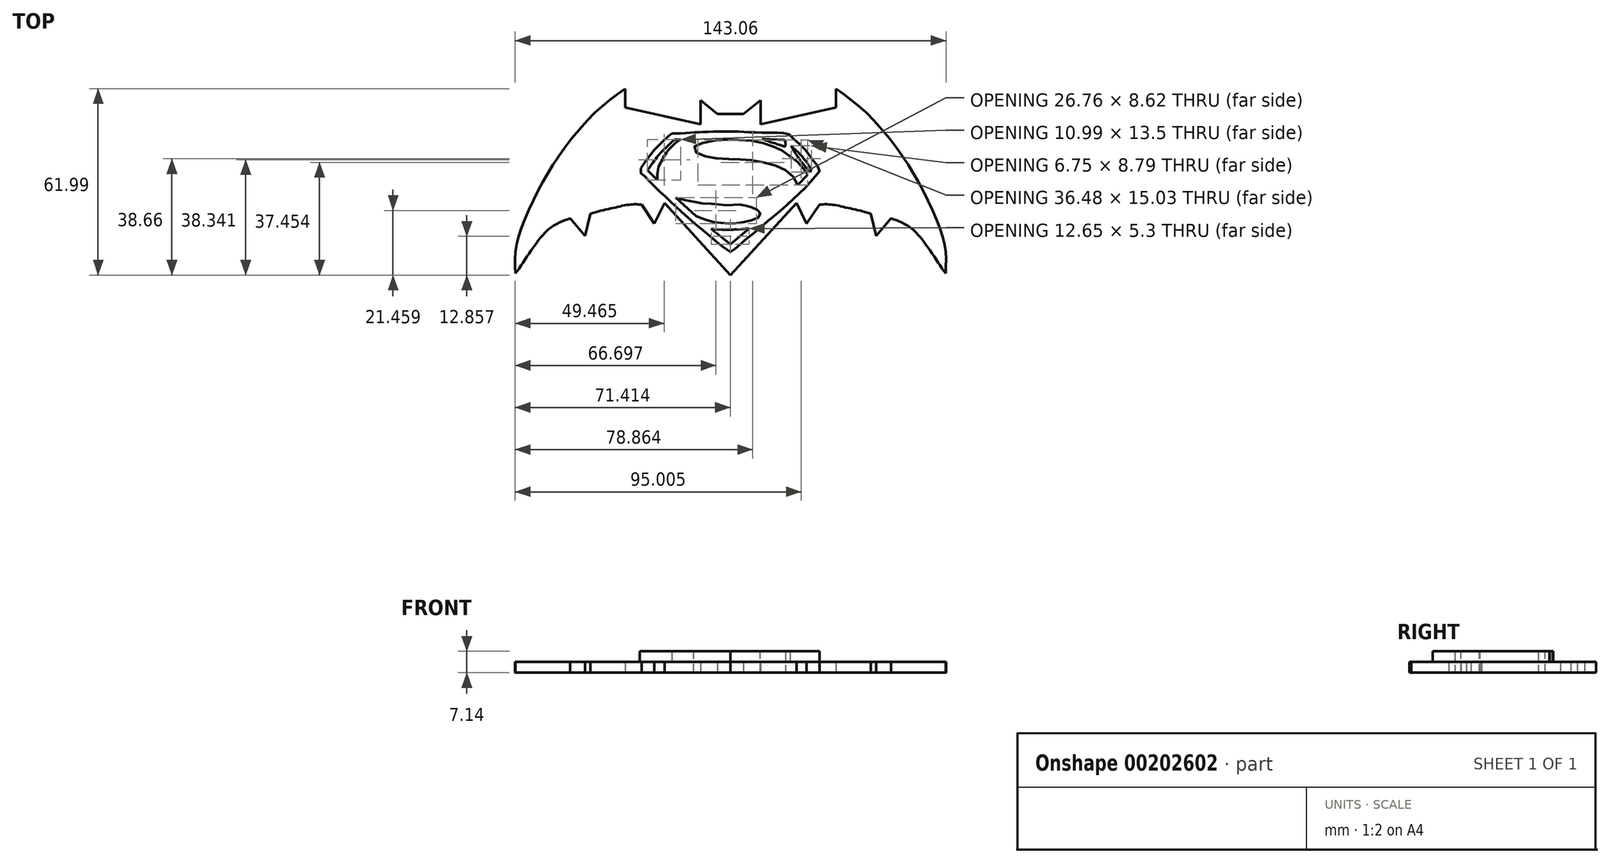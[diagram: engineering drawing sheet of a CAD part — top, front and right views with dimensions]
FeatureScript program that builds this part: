
annotation { "Feature Type Name" : "Feature", "Feature Type Description" : "" }
export const myFeature = defineFeature(function(context is Context, id is Id, definition is map)
    precondition{}
    {
        {
            var Q0;
            Q0=qCreatedBy(makeId("Top.planeOp"),FACE);
            var sketch = newSketch(context, id + "F0", { "sketchPlane" : qUnion([Q0])});
            skLineSegment(sketch, "E0", {"start": v(0, -29.29) * mm, "end": v(-21.94, -5.3) * mm});
            skLineSegment(sketch, "E1", {"start": v(-21.94, -5.3) * mm, "end": v(-25.27, -12.15) * mm});
            skLineSegment(sketch, "E2", {"start": v(-25.27, -12.15) * mm, "end": v(-29.54, -5.84) * mm});
            skFitSpline(sketch, "E3", {"points": [v(-29.54, -5.84) * mm, v(-33.44, -5.84) * mm, v(-39.05, -6.98) * mm, v(-46.5, -8.89) * mm], "startDerivative": vector(-13.8, 0.93) * mm, "endDerivative": vector(-19.94, -6.94) * mm});
            skLineSegment(sketch, "E4", {"start": v(-46.5, -8.89) * mm, "end": v(-48.35, -16.27) * mm});
            skLineSegment(sketch, "E5", {"start": v(-48.35, -16.27) * mm, "end": v(-53.26, -10.46) * mm});
            skFitSpline(sketch, "E6", {"points": [v(-53.26, -10.46) * mm, v(-56.7, -11.7) * mm, v(-60.93, -14.52) * mm, v(-65.15, -19.53) * mm, v(-68.59, -24.69) * mm, v(-71.4, -28.75) * mm], "startDerivative": vector(-20.24, -6.27) * mm, "endDerivative": vector(-14.3, -20.24) * mm});
            skFitSpline(sketch, "E7", {"points": [v(-71.4, -28.75) * mm, v(-71.4, -21.87) * mm, v(-69.37, -13.43) * mm, v(-63.27, 0) * mm, v(-56.23, 11.43) * mm, v(-44.98, 24.73) * mm, v(-34.97, 32.7) * mm], "startDerivative": vector(-2.55, 54.29) * mm, "endDerivative": vector(57.68, 41.15) * mm});
            skLineSegment(sketch, "E8", {"start": v(-34.97, 32.7) * mm, "end": v(-34.97, 26.45) * mm});
            skLineSegment(sketch, "E9", {"start": v(-34.97, 26.45) * mm, "end": v(-9.95, 20.82) * mm});
            skLineSegment(sketch, "E10", {"start": v(-9.95, 20.82) * mm, "end": v(-9.95, 28.8) * mm});
            skLineSegment(sketch, "E11", {"start": v(-9.95, 28.8) * mm, "end": v(-4.32, 24.26) * mm});
            skLineSegment(sketch, "E12", {"start": v(-4.32, 24.26) * mm, "end": v(0, 24.26) * mm});
            skLineSegment(sketch, "E13.MirrorCS", {"start": v(4.32, 24.26) * mm, "end": v(0, 24.26) * mm});
            skLineSegment(sketch, "E14.MirrorCS", {"start": v(9.95, 28.8) * mm, "end": v(4.32, 24.26) * mm});
            skLineSegment(sketch, "E15.MirrorCS", {"start": v(9.95, 20.82) * mm, "end": v(9.95, 28.8) * mm});
            skLineSegment(sketch, "E16.MirrorCS", {"start": v(34.97, 26.45) * mm, "end": v(9.95, 20.82) * mm});
            skLineSegment(sketch, "E17.MirrorCS", {"start": v(34.97, 32.7) * mm, "end": v(34.97, 26.45) * mm});
            skFitSpline(sketch, "E18.MirrorCS", {"points": [v(71.4, -28.75) * mm, v(71.4, -21.87) * mm, v(69.37, -13.43) * mm, v(63.27, 0) * mm, v(56.23, 11.43) * mm, v(44.98, 24.73) * mm, v(34.97, 32.7) * mm], "startDerivative": vector(2.55, 54.29) * mm, "endDerivative": vector(-57.68, 41.15) * mm});
            skFitSpline(sketch, "E19.MirrorCS", {"points": [v(53.26, -10.46) * mm, v(56.7, -11.7) * mm, v(60.93, -14.52) * mm, v(65.15, -19.53) * mm, v(68.59, -24.69) * mm, v(71.4, -28.75) * mm], "startDerivative": vector(20.24, -6.27) * mm, "endDerivative": vector(14.3, -20.24) * mm});
            skLineSegment(sketch, "E20.MirrorCS", {"start": v(48.35, -16.27) * mm, "end": v(53.26, -10.46) * mm});
            skLineSegment(sketch, "E21.MirrorCS", {"start": v(46.5, -8.89) * mm, "end": v(48.35, -16.27) * mm});
            skFitSpline(sketch, "E22.MirrorCS", {"points": [v(29.54, -5.84) * mm, v(33.44, -5.84) * mm, v(39.05, -6.98) * mm, v(46.5, -8.89) * mm], "startDerivative": vector(13.8, 0.93) * mm, "endDerivative": vector(19.94, -6.94) * mm});
            skLineSegment(sketch, "E23.MirrorCS", {"start": v(25.27, -12.15) * mm, "end": v(29.54, -5.84) * mm});
            skLineSegment(sketch, "E24.MirrorCS", {"start": v(21.94, -5.3) * mm, "end": v(25.27, -12.15) * mm});
            skLineSegment(sketch, "E25.MirrorCS", {"start": v(0, -29.29) * mm, "end": v(21.94, -5.3) * mm});
            skFitSpline(sketch, "E26", {"points": [v(-6.44, -13.95) * mm, v(-5.68, -14) * mm, v(-4.34, -14.09) * mm, v(-2.2, -14.18) * mm, v(0, -14.17) * mm, v(2.5, -14.06) * mm, v(5.6, -13.82) * mm, v(6.2, -13.78) * mm], "startDerivative": vector(7.48, -0.48) * mm, "endDerivative": vector(5.5, 0.3) * mm});
            skLineSegment(sketch, "E27", {"start": v(-6.44, -13.95) * mm, "end": v(0, -19.08) * mm});
            skLineSegment(sketch, "E28", {"start": v(0, -19.08) * mm, "end": v(6.2, -13.78) * mm});
            skLineSegment(sketch, "E29", {"start": v(-18.21, -3.52) * mm, "end": v(-11.46, -9.7) * mm});
            skFitSpline(sketch, "E30", {"points": [v(-11.46, -9.7) * mm, v(-10.56, -10.1) * mm, v(-8.56, -10.77) * mm, v(-6.1, -11.55) * mm, v(-3.86, -11.88) * mm, v(-0.33, -12.15) * mm, v(1.86, -12.1) * mm, v(5, -11.58) * mm, v(8.21, -10.65) * mm, v(9.66, -9.7) * mm, v(9.77, -8.65) * mm, v(9.15, -7.83) * mm, v(7.82, -7.04) * mm, v(5.86, -6.44) * mm, v(4.25, -6.01) * mm, v(2.15, -5.88) * mm, v(0, -6) * mm, v(-2.41, -6.01) * mm, v(-5.3, -5.7) * mm, v(-9.23, -5.41) * mm, v(-12.19, -4.88) * mm, v(-14.4, -4.47) * mm, v(-16.82, -3.98) * mm, v(-18.21, -3.52) * mm], "startDerivative": vector(27.77, -13.95) * mm, "endDerivative": vector(-35.91, 13.18) * mm});
            skLineSegment(sketch, "E31", {"start": v(25.58, 4.09) * mm, "end": v(22.35, 0.65) * mm});
            skFitSpline(sketch, "E32", {"points": [v(25.58, 4.09) * mm, v(24.77, 5.23) * mm, v(23.54, 6.93) * mm, v(21.88, 8.58) * mm, v(20.02, 10.03) * mm, v(17.64, 11.77) * mm, v(14.97, 13.08) * mm, v(12.89, 13.97) * mm, v(9.02, 14.95) * mm, v(5.25, 15.5) * mm, v(0.62, 15.67) * mm, v(-2.1, 15.67) * mm, v(-7.57, 15.08) * mm, v(-10.88, 14.1) * mm, v(-12.07, 13.3) * mm, v(-12.07, 12.1) * mm, v(-10.03, 10.7) * mm, v(-7.19, 9.94) * mm, v(-3.41, 9.4) * mm, v(1.09, 9.26) * mm, v(4.27, 9.05) * mm, v(8.05, 8.71) * mm, v(12.46, 7.82) * mm, v(16.28, 6.63) * mm, v(19.04, 5.06) * mm, v(21.16, 3.07) * mm, v(22.35, 0.65) * mm], "startDerivative": vector(-29.55, 41.43) * mm, "endDerivative": vector(27.27, -69.59) * mm});
            skLineSegment(sketch, "E33", {"start": v(-16.57, 15.8) * mm, "end": v(-18.6, 15.8) * mm});
            skFitSpline(sketch, "E34", {"points": [v(-18.6, 15.8) * mm, v(-19.41, 15.04) * mm, v(-21.11, 13.42) * mm, v(-22.72, 11.8) * mm, v(-24.12, 10.28) * mm, v(-26.2, 7.52) * mm, v(-27.56, 5.61) * mm], "startDerivative": vector(-6.15, -5.84) * mm, "endDerivative": vector(-7.3, -10.34) * mm});
            skPoint(sketch, "E35.1.internal.snap0", {"position": v(-17.59, 15.8) * mm});
            skFitSpline(sketch, "E35", {"points": [v(-16.57, 15.8) * mm, v(-17.59, 15.16) * mm, v(-19.5, 13.47) * mm, v(-20.86, 11.94) * mm, v(-22.13, 10.11) * mm, v(-23.19, 8.16) * mm, v(-24.08, 6) * mm, v(-24.34, 2.3) * mm], "startDerivative": vector(-9.04, -4.99) * mm, "endDerivative": vector(-0.07, -21.77) * mm});
            skLineSegment(sketch, "E36", {"start": v(-27.56, 5.61) * mm, "end": v(-24.34, 2.3) * mm});
            skLineSegment(sketch, "E37", {"start": v(10.47, 16.01) * mm, "end": v(17.98, 15.59) * mm});
            skPoint(sketch, "E38.4.internal.snap0", {"position": v(14.22, 15.8) * mm});
            skFitSpline(sketch, "E38", {"points": [v(17.98, 15.59) * mm, v(18.28, 14.14) * mm, v(17.98, 13.47) * mm, v(16.8, 13.85) * mm, v(14.22, 14.61) * mm, v(10.47, 16.01) * mm], "startDerivative": vector(2.6, -8.42) * mm, "endDerivative": vector(-13.23, 5.37) * mm});
            skFitSpline(sketch, "E39", {"points": [v(20.1, 13.76) * mm, v(20.61, 12.7) * mm, v(21.84, 10.66) * mm, v(22.99, 9.18) * mm, v(24.35, 7.31) * mm, v(26.3, 4.98) * mm], "startDerivative": vector(2.89, -6.42) * mm, "endDerivative": vector(8.55, -9.8) * mm});
            skFitSpline(sketch, "E40", {"points": [v(20.1, 13.76) * mm, v(21.29, 12.57) * mm, v(22.94, 11) * mm, v(24.39, 9.3) * mm, v(25.62, 7.7) * mm, v(26.85, 5.61) * mm], "startDerivative": vector(6.3, -6.5) * mm, "endDerivative": vector(5.65, -10.17) * mm});
            skLineSegment(sketch, "E41", {"start": v(26.85, 5.61) * mm, "end": v(26.3, 4.98) * mm});
            skFitSpline(sketch, "E42", {"points": [v(-19.5, 17.75) * mm, v(-16.57, 17.82) * mm, v(-12.84, 18.1) * mm, v(-10.21, 18.23) * mm, v(-6.57, 18.37) * mm, v(-2.93, 18.38) * mm, v(1.24, 18.45) * mm, v(5.69, 18.25) * mm, v(12.23, 18.05) * mm, v(18.9, 17.65) * mm, v(19.7, 17.11) * mm], "startDerivative": vector(31.61, 0.2) * mm, "endDerivative": vector(10.75, -11.7) * mm});
            skFitSpline(sketch, "E43", {"points": [v(19.7, 17.11) * mm, v(22.13, 14.88) * mm, v(25.23, 11.85) * mm, v(27.25, 9.08) * mm, v(29.54, 5.7) * mm, v(27.86, 3.26) * mm, v(24.35, -0.66) * mm, v(20.58, -4.25) * mm, v(15.66, -8.65) * mm, v(11.55, -12.04) * mm, v(7.85, -15.22) * mm, v(4.88, -17.59) * mm, v(2.12, -20.1) * mm, v(0, -21.58) * mm], "startDerivative": vector(33.55, -31.1) * mm, "endDerivative": vector(-34.43, -22) * mm});
            skFitSpline(sketch, "E44", {"points": [v(0, -21.58) * mm, v(-1.12, -20.9) * mm, v(-3.81, -18.95) * mm, v(-7.25, -15.98) * mm, v(-13.24, -10.98) * mm, v(-17.42, -7.2) * mm, v(-20.45, -4.3) * mm, v(-23.48, -1.52) * mm, v(-26.58, 1.45) * mm, v(-28.6, 3.61) * mm, v(-30.09, 5.16) * mm, v(-28.74, 7.73) * mm, v(-26.11, 11.46) * mm, v(-21, 16.6) * mm, v(-19.5, 17.75) * mm], "startDerivative": vector(-23.99, 13.8) * mm, "endDerivative": vector(24.49, 17.4) * mm});
            skSolve(sketch);
        }
        {
            var Q0;
            Q0=makeQuery(id+"F0.imprint","IMPRINT",FACE,{"disambiguationData":[TD([[makeQuery(id+"F0.imprint","IMPRINT",EDGE,{"derivedFrom":sQuery(id+"F0.wireOp",EDGE,"E26")}),1.0]])]});
            extrude(context, id + "F1", {"entities" : qUnion([Q0]), "depth" : 7.14 * mm});
        }
        {
            var Q0;
            Q0 = qSketchRegion(id + "F0", true);
            extrude(context, id + "F2", {"entities" : qUnion([Q0]), "operationType" : NewBodyOperationType.ADD, "depth" : 3.56 * mm});
        }
    });
